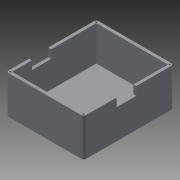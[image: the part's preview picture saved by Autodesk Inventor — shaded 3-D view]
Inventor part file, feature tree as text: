
AUTODESK INVENTOR PART (.ipt)
format: ipt  version: 2015 (Build 190159000, 159)  size: 134,656 bytes
history: native  units: in
note: dims shown in document units (in); Inventor stores cm internally (conversion verified against a paired STEP export)
features: extrude x4, sketch x4, shell x1, fillet x1
ambient origin geometry x8: Origin, YZ Plane, XZ Plane, XY Plane, X Axis, Y Axis, Z Axis, Center Point
bodies: Body1 (feature_tree)
feature tree (10):
  extrude  "Extrusion2"  Depth=3.622in
  shell  "Shell2"  Thickness=1.7717in
  fillet  "Fillet1"  Radius=0.1378in
  extrude  "Extrusion3"  Depth=0.1181in
  extrude  "Extrusion5"  Depth=0.0984in
  extrude  "Extrusion6"  Depth=0.0394in
  sketch  "Sketch2"  dims[d28=4.2126in d29=3.622in d30=1.7717in d31=0.0in d32=0.1378in]
  sketch  "Sketch3"  dims[d33=0.1181in d34=0.0787in]
  sketch  "Sketch9"  dims[d35=0.0984in d36=0.0984in]
  sketch  "Sketch10"  dims[d37=1.811in d38=2.1063in d39=0.2756in d40=0.0in d102=0.3937in d103=1.5374in d104=1.7539in d105=0.0in d106=0.315in d107=0.0in d108=1.065in d109=0.0in d110=2.2461in d111=0.3937in d112=0.315in d113=0.0in d61=0.0394in d62=0.0394in]
